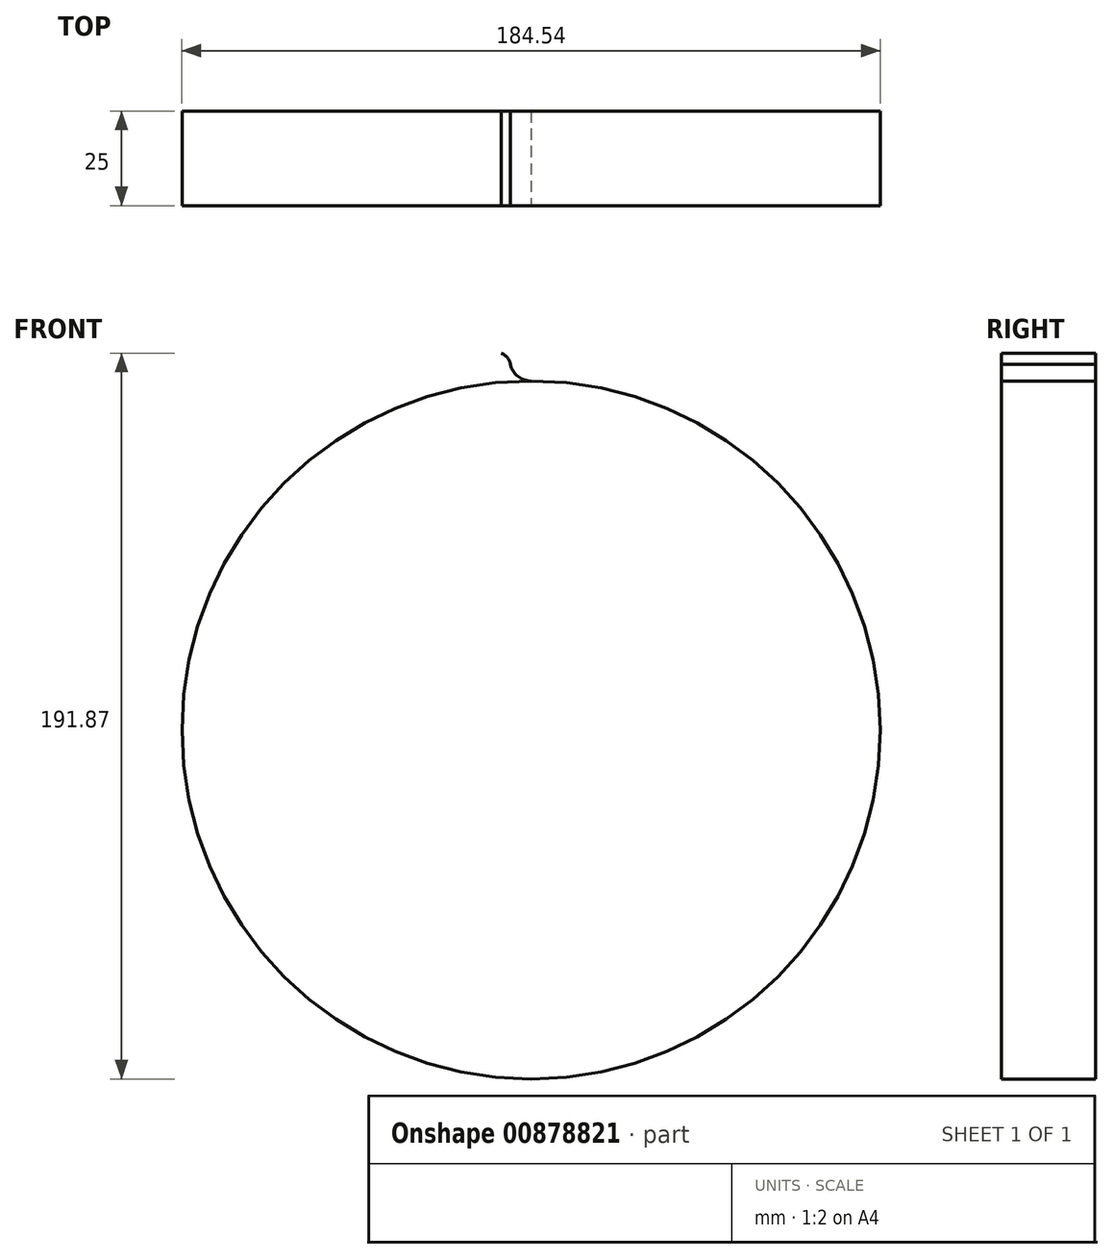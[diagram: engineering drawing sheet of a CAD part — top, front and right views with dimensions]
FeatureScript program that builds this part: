
annotation { "Feature Type Name" : "Feature", "Feature Type Description" : "" }
export const myFeature = defineFeature(function(context is Context, id is Id, definition is map)
    precondition{}
    {
        {
            var Q0;
            Q0=qCreatedBy(makeId("Front.planeOp"),FACE);
            var sketch = newSketch(context, id + "F0", { "sketchPlane" : qUnion([Q0])});
            skCircle(sketch, "E0", {"center": v(0, 0) * mm, "radius": 92.27 * mm});
            skSolve(sketch);
        }
        {
            var Q0;
            Q0=qCreatedBy(makeId("Front.planeOp"),FACE);
            var sketch = newSketch(context, id + "F1", { "sketchPlane" : qUnion([Q0])});
            skArc(sketch, "E1", {"start": v(-5.45, 96.6) * mm, "mid": v(-3.48, 93.48) * mm, "end": v(0, 92.22) * mm});
            skArc(sketch, "E2", {"start": v(-5.45, 96.6) * mm, "mid": v(-6.27, 98.44) * mm, "end": v(-7.91, 99.6) * mm});
            skSolve(sketch);
        }
        {
            var Q0;
            Q0=qCreatedBy(makeId("Right.planeOp"),FACE);
            var sketch = newSketch(context, id + "F2", { "sketchPlane" : qUnion([Q0])});
            skLineSegment(sketch, "E3", {"start": v(52.73, 0) * mm, "end": v(-26.92, 0) * mm});
            skSolve(sketch);
        }
        {
            var Q0;
            Q0=sQuery(id+"FXEql6IQrDPzo9p_0.5.F1.wireOp",EDGE,"E2");
            var Q1;
            Q1=sQuery(id+"FXEql6IQrDPzo9p_0.4.F1.wireOp",EDGE,"E2");
            var Q2;
            Q2=sQuery(id+"FXEql6IQrDPzo9p_0.6.F1.wireOp",EDGE,"E2");
            var Q3;
            Q3=sQuery(id+"FXEql6IQrDPzo9p_0.7.F1.wireOp",EDGE,"E2");
            var Q4;
            Q4=sQuery(id+"FXEql6IQrDPzo9p_0.8.F1.wireOp",EDGE,"E2");
            var Q5;
            Q5=sQuery(id+"FXEql6IQrDPzo9p_0.31.FfP7r1bTpHOR9mC_0.1.F1.wireOp",EDGE,"E1");
            var Q6;
            Q6=sQuery(id+"FXEql6IQrDPzo9p_0.32.FfP7r1bTpHOR9mC_0.1.F1.wireOp",EDGE,"E1");
            var Q7;
            Q7=sQuery(id+"FXEql6IQrDPzo9p_0.33.FfP7r1bTpHOR9mC_0.1.F1.wireOp",EDGE,"E1");
            var Q8;
            Q8=sQuery(id+"FXEql6IQrDPzo9p_0.34.FfP7r1bTpHOR9mC_0.1.F1.wireOp",EDGE,"E1");
            var Q9;
            Q9=sQuery(id+"FXEql6IQrDPzo9p_0.35.FfP7r1bTpHOR9mC_0.1.F1.wireOp",EDGE,"E1");
            var Q10;
            Q10=sQuery(id+"FXEql6IQrDPzo9p_0.36.FfP7r1bTpHOR9mC_0.1.F1.wireOp",EDGE,"E1");
            var Q11;
            Q11=sQuery(id+"FXEql6IQrDPzo9p_0.3.F1.wireOp",EDGE,"E2");
            var Q12;
            Q12=sQuery(id+"FXEql6IQrDPzo9p_0.37.FfP7r1bTpHOR9mC_0.1.F1.wireOp",EDGE,"E1");
            var Q13;
            Q13=sQuery(id+"FXEql6IQrDPzo9p_0.2.F1.wireOp",EDGE,"E2");
            var Q14;
            Q14=sQuery(id+"FXEql6IQrDPzo9p_0.38.FfP7r1bTpHOR9mC_0.1.F1.wireOp",EDGE,"E1");
            var Q15;
            Q15=sQuery(id+"FXEql6IQrDPzo9p_0.1.F1.wireOp",EDGE,"E2");
            var Q16;
            Q16=sQuery(id+"FXEql6IQrDPzo9p_0.39.FfP7r1bTpHOR9mC_0.1.F1.wireOp",EDGE,"E1");
            var Q17;
            Q17=sQuery(id+"F1.wireOp",EDGE,"E2");
            var Q18;
            Q18=sQuery(id+"FfP7r1bTpHOR9mC_0.1.F1.wireOp",EDGE,"E1");
            var Q19;
            Q19=sQuery(id+"FXEql6IQrDPzo9p_0.39.F1.wireOp",EDGE,"E2");
            var Q20;
            Q20=sQuery(id+"FXEql6IQrDPzo9p_0.1.FfP7r1bTpHOR9mC_0.1.F1.wireOp",EDGE,"E1");
            var Q21;
            Q21=sQuery(id+"FXEql6IQrDPzo9p_0.38.F1.wireOp",EDGE,"E2");
            var Q22;
            Q22=sQuery(id+"FXEql6IQrDPzo9p_0.2.FfP7r1bTpHOR9mC_0.1.F1.wireOp",EDGE,"E1");
            var Q23;
            Q23=sQuery(id+"FXEql6IQrDPzo9p_0.37.F1.wireOp",EDGE,"E2");
            var Q24;
            Q24=sQuery(id+"FXEql6IQrDPzo9p_0.3.FfP7r1bTpHOR9mC_0.1.F1.wireOp",EDGE,"E1");
            var Q25;
            Q25=sQuery(id+"FXEql6IQrDPzo9p_0.36.F1.wireOp",EDGE,"E2");
            var Q26;
            Q26=sQuery(id+"FXEql6IQrDPzo9p_0.4.FfP7r1bTpHOR9mC_0.1.F1.wireOp",EDGE,"E1");
            var Q27;
            Q27=sQuery(id+"FXEql6IQrDPzo9p_0.35.F1.wireOp",EDGE,"E2");
            var Q28;
            Q28=sQuery(id+"FXEql6IQrDPzo9p_0.5.FfP7r1bTpHOR9mC_0.1.F1.wireOp",EDGE,"E1");
            var Q29;
            Q29=sQuery(id+"FXEql6IQrDPzo9p_0.34.F1.wireOp",EDGE,"E2");
            var Q30;
            Q30=sQuery(id+"FXEql6IQrDPzo9p_0.6.FfP7r1bTpHOR9mC_0.1.F1.wireOp",EDGE,"E1");
            var Q31;
            Q31=sQuery(id+"FXEql6IQrDPzo9p_0.7.FfP7r1bTpHOR9mC_0.1.F1.wireOp",EDGE,"E1");
            var Q32;
            Q32=sQuery(id+"FXEql6IQrDPzo9p_0.32.F1.wireOp",EDGE,"E2");
            var Q33;
            Q33=sQuery(id+"FXEql6IQrDPzo9p_0.33.F1.wireOp",EDGE,"E2");
            var Q34;
            Q34=sQuery(id+"FXEql6IQrDPzo9p_0.8.FfP7r1bTpHOR9mC_0.1.F1.wireOp",EDGE,"E1");
            var Q35;
            Q35=sQuery(id+"FXEql6IQrDPzo9p_0.31.F1.wireOp",EDGE,"E2");
            var Q36;
            Q36=sQuery(id+"FXEql6IQrDPzo9p_0.9.FfP7r1bTpHOR9mC_0.1.F1.wireOp",EDGE,"E1");
            var Q37;
            Q37=sQuery(id+"FXEql6IQrDPzo9p_0.30.F1.wireOp",EDGE,"E2");
            var Q38;
            Q38=sQuery(id+"FXEql6IQrDPzo9p_0.10.FfP7r1bTpHOR9mC_0.1.F1.wireOp",EDGE,"E1");
            var Q39;
            Q39=sQuery(id+"FXEql6IQrDPzo9p_0.29.F1.wireOp",EDGE,"E2");
            var Q40;
            Q40=sQuery(id+"FXEql6IQrDPzo9p_0.11.FfP7r1bTpHOR9mC_0.1.F1.wireOp",EDGE,"E1");
            var Q41;
            Q41=sQuery(id+"FXEql6IQrDPzo9p_0.28.F1.wireOp",EDGE,"E2");
            var Q42;
            Q42=sQuery(id+"FXEql6IQrDPzo9p_0.12.FfP7r1bTpHOR9mC_0.1.F1.wireOp",EDGE,"E1");
            var Q43;
            Q43=sQuery(id+"FXEql6IQrDPzo9p_0.27.F1.wireOp",EDGE,"E2");
            var Q44;
            Q44=sQuery(id+"FXEql6IQrDPzo9p_0.13.FfP7r1bTpHOR9mC_0.1.F1.wireOp",EDGE,"E1");
            var Q45;
            Q45=sQuery(id+"FXEql6IQrDPzo9p_0.26.F1.wireOp",EDGE,"E2");
            var Q46;
            Q46=sQuery(id+"FXEql6IQrDPzo9p_0.14.FfP7r1bTpHOR9mC_0.1.F1.wireOp",EDGE,"E1");
            var Q47;
            Q47=sQuery(id+"FXEql6IQrDPzo9p_0.25.F1.wireOp",EDGE,"E2");
            var Q48;
            Q48=sQuery(id+"FXEql6IQrDPzo9p_0.15.FfP7r1bTpHOR9mC_0.1.F1.wireOp",EDGE,"E1");
            var Q49;
            Q49=sQuery(id+"FXEql6IQrDPzo9p_0.24.F1.wireOp",EDGE,"E2");
            var Q50;
            Q50=sQuery(id+"FXEql6IQrDPzo9p_0.16.FfP7r1bTpHOR9mC_0.1.F1.wireOp",EDGE,"E1");
            var Q51;
            Q51=sQuery(id+"FXEql6IQrDPzo9p_0.23.F1.wireOp",EDGE,"E2");
            var Q52;
            Q52=sQuery(id+"FXEql6IQrDPzo9p_0.17.FfP7r1bTpHOR9mC_0.1.F1.wireOp",EDGE,"E1");
            var Q53;
            Q53=sQuery(id+"FXEql6IQrDPzo9p_0.22.F1.wireOp",EDGE,"E2");
            var Q54;
            Q54=sQuery(id+"FXEql6IQrDPzo9p_0.18.FfP7r1bTpHOR9mC_0.1.F1.wireOp",EDGE,"E1");
            var Q55;
            Q55=sQuery(id+"FXEql6IQrDPzo9p_0.21.F1.wireOp",EDGE,"E2");
            var Q56;
            Q56=sQuery(id+"FXEql6IQrDPzo9p_0.19.FfP7r1bTpHOR9mC_0.1.F1.wireOp",EDGE,"E1");
            var Q57;
            Q57=sQuery(id+"FXEql6IQrDPzo9p_0.20.F1.wireOp",EDGE,"E2");
            var Q58;
            Q58=sQuery(id+"FXEql6IQrDPzo9p_0.19.F1.wireOp",EDGE,"E2");
            var Q59;
            Q59=sQuery(id+"FXEql6IQrDPzo9p_0.20.FfP7r1bTpHOR9mC_0.1.F1.wireOp",EDGE,"E1");
            var Q60;
            Q60=sQuery(id+"FXEql6IQrDPzo9p_0.21.FfP7r1bTpHOR9mC_0.1.F1.wireOp",EDGE,"E1");
            var Q61;
            Q61=sQuery(id+"FXEql6IQrDPzo9p_0.18.F1.wireOp",EDGE,"E2");
            var Q62;
            Q62=sQuery(id+"FXEql6IQrDPzo9p_0.22.FfP7r1bTpHOR9mC_0.1.F1.wireOp",EDGE,"E1");
            var Q63;
            Q63=sQuery(id+"FXEql6IQrDPzo9p_0.17.F1.wireOp",EDGE,"E2");
            var Q64;
            Q64=sQuery(id+"FXEql6IQrDPzo9p_0.23.FfP7r1bTpHOR9mC_0.1.F1.wireOp",EDGE,"E1");
            var Q65;
            Q65=sQuery(id+"FXEql6IQrDPzo9p_0.16.F1.wireOp",EDGE,"E2");
            var Q66;
            Q66=sQuery(id+"FXEql6IQrDPzo9p_0.24.FfP7r1bTpHOR9mC_0.1.F1.wireOp",EDGE,"E1");
            var Q67;
            Q67=sQuery(id+"FXEql6IQrDPzo9p_0.15.F1.wireOp",EDGE,"E2");
            var Q68;
            Q68=sQuery(id+"FXEql6IQrDPzo9p_0.25.FfP7r1bTpHOR9mC_0.1.F1.wireOp",EDGE,"E1");
            var Q69;
            Q69=sQuery(id+"FXEql6IQrDPzo9p_0.14.F1.wireOp",EDGE,"E2");
            var Q70;
            Q70=sQuery(id+"FXEql6IQrDPzo9p_0.26.FfP7r1bTpHOR9mC_0.1.F1.wireOp",EDGE,"E1");
            var Q71;
            Q71=sQuery(id+"FXEql6IQrDPzo9p_0.13.F1.wireOp",EDGE,"E2");
            var Q72;
            Q72=sQuery(id+"FXEql6IQrDPzo9p_0.27.FfP7r1bTpHOR9mC_0.1.F1.wireOp",EDGE,"E1");
            var Q73;
            Q73=sQuery(id+"FXEql6IQrDPzo9p_0.12.F1.wireOp",EDGE,"E2");
            var Q74;
            Q74=sQuery(id+"FXEql6IQrDPzo9p_0.28.FfP7r1bTpHOR9mC_0.1.F1.wireOp",EDGE,"E1");
            var Q75;
            Q75=sQuery(id+"FXEql6IQrDPzo9p_0.29.FfP7r1bTpHOR9mC_0.1.F1.wireOp",EDGE,"E2");
            var Q76;
            Q76=sQuery(id+"FXEql6IQrDPzo9p_0.10.F1.wireOp",EDGE,"E1");
            var Q77;
            Q77=sQuery(id+"FXEql6IQrDPzo9p_0.30.FfP7r1bTpHOR9mC_0.1.F1.wireOp",EDGE,"E2");
            var Q78;
            Q78=sQuery(id+"FXEql6IQrDPzo9p_0.9.F1.wireOp",EDGE,"E1");
            var Q79;
            Q79=sQuery(id+"FXEql6IQrDPzo9p_0.11.F1.wireOp",EDGE,"E1");
            var Q80;
            Q80=sQuery(id+"FXEql6IQrDPzo9p_0.30.FfP7r1bTpHOR9mC_0.1.F1.wireOp",EDGE,"E1");
            var Q81;
            Q81=sQuery(id+"FXEql6IQrDPzo9p_0.29.FfP7r1bTpHOR9mC_0.1.F1.wireOp",EDGE,"E1");
            var Q82;
            Q82=sQuery(id+"FXEql6IQrDPzo9p_0.12.F1.wireOp",EDGE,"E1");
            var Q83;
            Q83=sQuery(id+"FXEql6IQrDPzo9p_0.13.F1.wireOp",EDGE,"E1");
            var Q84;
            Q84=sQuery(id+"FXEql6IQrDPzo9p_0.14.F1.wireOp",EDGE,"E1");
            var Q85;
            Q85=sQuery(id+"FXEql6IQrDPzo9p_0.8.F1.wireOp",EDGE,"E1");
            var Q86;
            Q86=sQuery(id+"FXEql6IQrDPzo9p_0.7.F1.wireOp",EDGE,"E1");
            var Q87;
            Q87=sQuery(id+"FXEql6IQrDPzo9p_0.6.F1.wireOp",EDGE,"E1");
            var Q88;
            Q88=sQuery(id+"FXEql6IQrDPzo9p_0.5.F1.wireOp",EDGE,"E1");
            var Q89;
            Q89=sQuery(id+"FXEql6IQrDPzo9p_0.4.F1.wireOp",EDGE,"E1");
            var Q90;
            Q90=sQuery(id+"FXEql6IQrDPzo9p_0.2.F1.wireOp",EDGE,"E1");
            var Q91;
            Q91=sQuery(id+"FXEql6IQrDPzo9p_0.1.F1.wireOp",EDGE,"E1");
            var Q92;
            Q92=sQuery(id+"F1.wireOp",EDGE,"E1");
            var Q93;
            Q93=sQuery(id+"FXEql6IQrDPzo9p_0.39.F1.wireOp",EDGE,"E1");
            var Q94;
            Q94=sQuery(id+"FXEql6IQrDPzo9p_0.38.F1.wireOp",EDGE,"E1");
            var Q95;
            Q95=sQuery(id+"FXEql6IQrDPzo9p_0.37.F1.wireOp",EDGE,"E1");
            var Q96;
            Q96=sQuery(id+"FXEql6IQrDPzo9p_0.36.F1.wireOp",EDGE,"E1");
            var Q97;
            Q97=sQuery(id+"FXEql6IQrDPzo9p_0.35.F1.wireOp",EDGE,"E1");
            var Q98;
            Q98=sQuery(id+"FXEql6IQrDPzo9p_0.34.F1.wireOp",EDGE,"E1");
            var Q99;
            Q99=sQuery(id+"FXEql6IQrDPzo9p_0.33.F1.wireOp",EDGE,"E1");
            var Q100;
            Q100=sQuery(id+"FXEql6IQrDPzo9p_0.32.F1.wireOp",EDGE,"E1");
            var Q101;
            Q101=sQuery(id+"FXEql6IQrDPzo9p_0.31.F1.wireOp",EDGE,"E1");
            var Q102;
            Q102=sQuery(id+"FXEql6IQrDPzo9p_0.30.F1.wireOp",EDGE,"E1");
            var Q103;
            Q103=sQuery(id+"FXEql6IQrDPzo9p_0.29.F1.wireOp",EDGE,"E1");
            var Q104;
            Q104=sQuery(id+"FXEql6IQrDPzo9p_0.28.F1.wireOp",EDGE,"E1");
            var Q105;
            Q105=sQuery(id+"FXEql6IQrDPzo9p_0.27.F1.wireOp",EDGE,"E1");
            var Q106;
            Q106=sQuery(id+"FXEql6IQrDPzo9p_0.26.F1.wireOp",EDGE,"E1");
            var Q107;
            Q107=sQuery(id+"FXEql6IQrDPzo9p_0.25.F1.wireOp",EDGE,"E1");
            var Q108;
            Q108=sQuery(id+"FXEql6IQrDPzo9p_0.24.F1.wireOp",EDGE,"E1");
            var Q109;
            Q109=sQuery(id+"FXEql6IQrDPzo9p_0.23.F1.wireOp",EDGE,"E1");
            var Q110;
            Q110=sQuery(id+"FXEql6IQrDPzo9p_0.22.F1.wireOp",EDGE,"E1");
            var Q111;
            Q111=sQuery(id+"FXEql6IQrDPzo9p_0.21.F1.wireOp",EDGE,"E1");
            var Q112;
            Q112=sQuery(id+"FXEql6IQrDPzo9p_0.20.F1.wireOp",EDGE,"E1");
            var Q113;
            Q113=sQuery(id+"FXEql6IQrDPzo9p_0.19.F1.wireOp",EDGE,"E1");
            var Q114;
            Q114=sQuery(id+"FXEql6IQrDPzo9p_0.18.F1.wireOp",EDGE,"E1");
            var Q115;
            Q115=sQuery(id+"FXEql6IQrDPzo9p_0.17.F1.wireOp",EDGE,"E1");
            var Q116;
            Q116=sQuery(id+"FXEql6IQrDPzo9p_0.16.F1.wireOp",EDGE,"E1");
            var Q117;
            Q117=sQuery(id+"FXEql6IQrDPzo9p_0.15.F1.wireOp",EDGE,"E1");
            var Q118;
            Q118=sQuery(id+"FXEql6IQrDPzo9p_0.11.F1.wireOp",EDGE,"E2");
            var Q119;
            Q119=sQuery(id+"FXEql6IQrDPzo9p_0.3.F1.wireOp",EDGE,"E1");
            extrude(context, id + "F3", {"bodyType" : ToolBodyType.SURFACE, "surfaceEntities" : qUnion([Q0, Q1, Q2, Q3, Q4, Q5, Q6, Q7, Q8, Q9, Q10, Q11, Q12, Q13, Q14, Q15, Q16, Q17, Q18, Q19, Q20, Q21, Q22, Q23, Q24, Q25, Q26, Q27, Q28, Q29, Q30, Q31, Q32, Q33, Q34, Q35, Q36, Q37, Q38, Q39, Q40, Q41, Q42, Q43, Q44, Q45, Q46, Q47, Q48, Q49, Q50, Q51, Q52, Q53, Q54, Q55, Q56, Q57, Q58, Q59, Q60, Q61, Q62, Q63, Q64, Q65, Q66, Q67, Q68, Q69, Q70, Q71, Q72, Q73, Q74, Q75, Q76, Q77, Q78, Q79, Q80, Q81, Q82, Q83, Q84, Q85, Q86, Q87, Q88, Q89, Q90, Q91, Q92, Q93, Q94, Q95, Q96, Q97, Q98, Q99, Q100, Q101, Q102, Q103, Q104, Q105, Q106, Q107, Q108, Q109, Q110, Q111, Q112, Q113, Q114, Q115, Q116, Q117, Q118, Q119]), "depth" : 25 * mm, "offsetDistance" : 25 * mm});
        }
        {
            var Q0;
            Q0=sQuery(id+"FXEql6IQrDPzo9p_0.7.FfP7r1bTpHOR9mC_0.1.F1.wireOp",EDGE,"E2");
            var Q1;
            Q1=sQuery(id+"FXEql6IQrDPzo9p_0.5.FfP7r1bTpHOR9mC_0.1.F1.wireOp",EDGE,"E2");
            var Q2;
            Q2=sQuery(id+"FXEql6IQrDPzo9p_0.6.FfP7r1bTpHOR9mC_0.1.F1.wireOp",EDGE,"E2");
            var Q3;
            Q3=sQuery(id+"FXEql6IQrDPzo9p_0.4.FfP7r1bTpHOR9mC_0.1.F1.wireOp",EDGE,"E2");
            var Q4;
            Q4=sQuery(id+"FXEql6IQrDPzo9p_0.3.FfP7r1bTpHOR9mC_0.1.F1.wireOp",EDGE,"E2");
            var Q5;
            Q5=sQuery(id+"FXEql6IQrDPzo9p_0.2.FfP7r1bTpHOR9mC_0.1.F1.wireOp",EDGE,"E2");
            var Q6;
            Q6=sQuery(id+"FXEql6IQrDPzo9p_0.1.FfP7r1bTpHOR9mC_0.1.F1.wireOp",EDGE,"E2");
            var Q7;
            Q7=sQuery(id+"FfP7r1bTpHOR9mC_0.1.F1.wireOp",EDGE,"E2");
            var Q8;
            Q8=sQuery(id+"FXEql6IQrDPzo9p_0.39.FfP7r1bTpHOR9mC_0.1.F1.wireOp",EDGE,"E2");
            var Q9;
            Q9=sQuery(id+"FXEql6IQrDPzo9p_0.38.FfP7r1bTpHOR9mC_0.1.F1.wireOp",EDGE,"E2");
            var Q10;
            Q10=sQuery(id+"FXEql6IQrDPzo9p_0.37.FfP7r1bTpHOR9mC_0.1.F1.wireOp",EDGE,"E2");
            var Q11;
            Q11=sQuery(id+"FXEql6IQrDPzo9p_0.36.FfP7r1bTpHOR9mC_0.1.F1.wireOp",EDGE,"E2");
            var Q12;
            Q12=sQuery(id+"FXEql6IQrDPzo9p_0.35.FfP7r1bTpHOR9mC_0.1.F1.wireOp",EDGE,"E2");
            var Q13;
            Q13=sQuery(id+"FXEql6IQrDPzo9p_0.34.FfP7r1bTpHOR9mC_0.1.F1.wireOp",EDGE,"E2");
            var Q14;
            Q14=sQuery(id+"FXEql6IQrDPzo9p_0.33.FfP7r1bTpHOR9mC_0.1.F1.wireOp",EDGE,"E2");
            var Q15;
            Q15=sQuery(id+"FXEql6IQrDPzo9p_0.32.FfP7r1bTpHOR9mC_0.1.F1.wireOp",EDGE,"E2");
            var Q16;
            Q16=sQuery(id+"FXEql6IQrDPzo9p_0.31.FfP7r1bTpHOR9mC_0.1.F1.wireOp",EDGE,"E2");
            var Q17;
            Q17=sQuery(id+"FXEql6IQrDPzo9p_0.9.F1.wireOp",EDGE,"E2");
            var Q18;
            Q18=sQuery(id+"FXEql6IQrDPzo9p_0.10.F1.wireOp",EDGE,"E2");
            var Q19;
            Q19=sQuery(id+"FXEql6IQrDPzo9p_0.27.FfP7r1bTpHOR9mC_0.1.F1.wireOp",EDGE,"E2");
            var Q20;
            Q20=sQuery(id+"FXEql6IQrDPzo9p_0.26.FfP7r1bTpHOR9mC_0.1.F1.wireOp",EDGE,"E2");
            var Q21;
            Q21=sQuery(id+"FXEql6IQrDPzo9p_0.25.FfP7r1bTpHOR9mC_0.1.F1.wireOp",EDGE,"E2");
            var Q22;
            Q22=sQuery(id+"FXEql6IQrDPzo9p_0.23.FfP7r1bTpHOR9mC_0.1.F1.wireOp",EDGE,"E2");
            var Q23;
            Q23=sQuery(id+"FXEql6IQrDPzo9p_0.22.FfP7r1bTpHOR9mC_0.1.F1.wireOp",EDGE,"E2");
            var Q24;
            Q24=sQuery(id+"FXEql6IQrDPzo9p_0.21.FfP7r1bTpHOR9mC_0.1.F1.wireOp",EDGE,"E2");
            var Q25;
            Q25=sQuery(id+"FXEql6IQrDPzo9p_0.20.FfP7r1bTpHOR9mC_0.1.F1.wireOp",EDGE,"E2");
            var Q26;
            Q26=sQuery(id+"FXEql6IQrDPzo9p_0.19.FfP7r1bTpHOR9mC_0.1.F1.wireOp",EDGE,"E2");
            var Q27;
            Q27=sQuery(id+"FXEql6IQrDPzo9p_0.18.FfP7r1bTpHOR9mC_0.1.F1.wireOp",EDGE,"E2");
            var Q28;
            Q28=sQuery(id+"FXEql6IQrDPzo9p_0.17.FfP7r1bTpHOR9mC_0.1.F1.wireOp",EDGE,"E2");
            var Q29;
            Q29=sQuery(id+"FXEql6IQrDPzo9p_0.16.FfP7r1bTpHOR9mC_0.1.F1.wireOp",EDGE,"E2");
            var Q30;
            Q30=sQuery(id+"FXEql6IQrDPzo9p_0.15.FfP7r1bTpHOR9mC_0.1.F1.wireOp",EDGE,"E2");
            var Q31;
            Q31=sQuery(id+"FXEql6IQrDPzo9p_0.14.FfP7r1bTpHOR9mC_0.1.F1.wireOp",EDGE,"E2");
            var Q32;
            Q32=sQuery(id+"FXEql6IQrDPzo9p_0.13.FfP7r1bTpHOR9mC_0.1.F1.wireOp",EDGE,"E2");
            var Q33;
            Q33=sQuery(id+"FXEql6IQrDPzo9p_0.12.FfP7r1bTpHOR9mC_0.1.F1.wireOp",EDGE,"E2");
            var Q34;
            Q34=sQuery(id+"FXEql6IQrDPzo9p_0.11.FfP7r1bTpHOR9mC_0.1.F1.wireOp",EDGE,"E2");
            var Q35;
            Q35=sQuery(id+"FXEql6IQrDPzo9p_0.10.FfP7r1bTpHOR9mC_0.1.F1.wireOp",EDGE,"E2");
            var Q36;
            Q36=sQuery(id+"FXEql6IQrDPzo9p_0.9.FfP7r1bTpHOR9mC_0.1.F1.wireOp",EDGE,"E2");
            var Q37;
            Q37=sQuery(id+"FXEql6IQrDPzo9p_0.8.FfP7r1bTpHOR9mC_0.1.F1.wireOp",EDGE,"E2");
            var Q38;
            Q38=sQuery(id+"F0.wireOp",EDGE,"E0");
            var Q39;
            Q39=sQuery(id+"FXEql6IQrDPzo9p_0.28.FfP7r1bTpHOR9mC_0.1.F1.wireOp",EDGE,"E2");
            var Q40;
            Q40=sQuery(id+"FXEql6IQrDPzo9p_0.24.FfP7r1bTpHOR9mC_0.1.F1.wireOp",EDGE,"E2");
            extrude(context, id + "F4", {"bodyType" : ToolBodyType.SURFACE, "surfaceEntities" : qUnion([Q0, Q1, Q2, Q3, Q4, Q5, Q6, Q7, Q8, Q9, Q10, Q11, Q12, Q13, Q14, Q15, Q16, Q17, Q18, Q19, Q20, Q21, Q22, Q23, Q24, Q25, Q26, Q27, Q28, Q29, Q30, Q31, Q32, Q33, Q34, Q35, Q36, Q37, Q38, Q39, Q40]), "depth" : 25 * mm, "offsetDistance" : 25 * mm});
        }
    });
